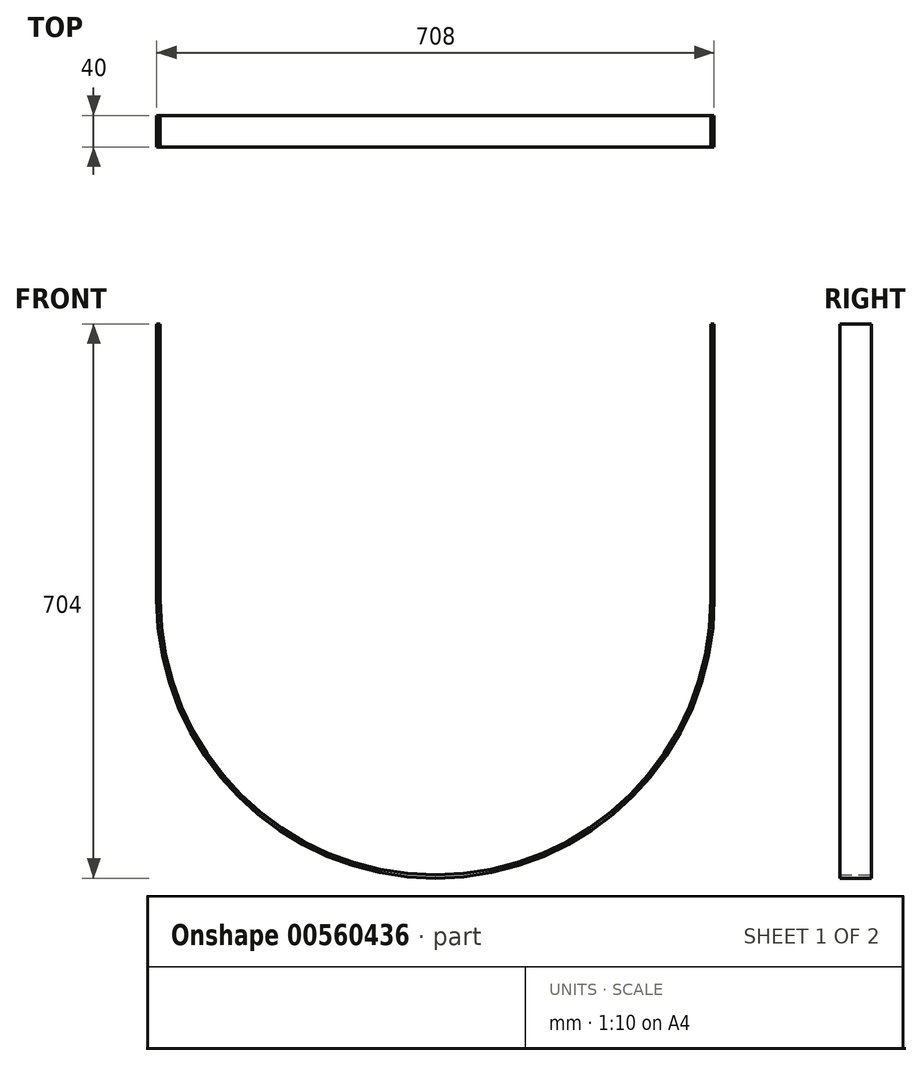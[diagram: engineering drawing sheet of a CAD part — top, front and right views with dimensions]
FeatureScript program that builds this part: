
annotation { "Feature Type Name" : "Feature", "Feature Type Description" : "" }
export const myFeature = defineFeature(function(context is Context, id is Id, definition is map)
    precondition{}
    {
        {
            var Q0;
            Q0=qCreatedBy(makeId("Front.planeOp"),FACE);
            var sketch = newSketch(context, id + "F0", { "sketchPlane" : qUnion([Q0])});
            skLineSegment(sketch, "E0", {"start": v(-350, 0) * mm, "end": v(-350, 350) * mm});
            skLineSegment(sketch, "E1", {"start": v(350, 0) * mm, "end": v(350, 350) * mm});
            skArc(sketch, "E2", {"start": v(-350, 0) * mm, "mid": v(0, -350) * mm, "end": v(350, 0) * mm});
            skLineSegment(sketch, "E3.0", {"start": v(354, 0) * mm, "end": v(354, 350) * mm});
            skArc(sketch, "E3.1", {"start": v(-354, 0) * mm, "mid": v(0, -354) * mm, "end": v(354, 0) * mm});
            skLineSegment(sketch, "E3.2", {"start": v(-354, 0) * mm, "end": v(-354, 350) * mm});
            skLineSegment(sketch, "E4", {"start": v(350, 350) * mm, "end": v(354, 350) * mm});
            skLineSegment(sketch, "E5", {"start": v(-354, 350) * mm, "end": v(-350, 350) * mm});
            skSolve(sketch);
        }
        {
            var Q0;
            Q0=makeQuery(id+"F0.imprint","IMPRINT",FACE,{"disambiguationData":[TD([[makeQuery(id+"F0.imprint","IMPRINT",EDGE,{"derivedFrom":sQuery(id+"F0.wireOp",EDGE,"E0")}),-1.0]])]});
            var Q1;
            Q1=makeQuery(id+"F0.imprint","IMPRINT",FACE,{"disambiguationData":[TD([[makeQuery(id+"F0.imprint","IMPRINT",EDGE,{"derivedFrom":sQuery(id+"F0.wireOp",EDGE,"E0")}),1.0]])]});
            extrude(context, id + "F1", {"entities" : qUnion([Q0, Q1]), "endBound" : BoundingType.SYMMETRIC, "depth" : 40 * mm, "offsetDistance" : 25 * mm});
        }
    });
